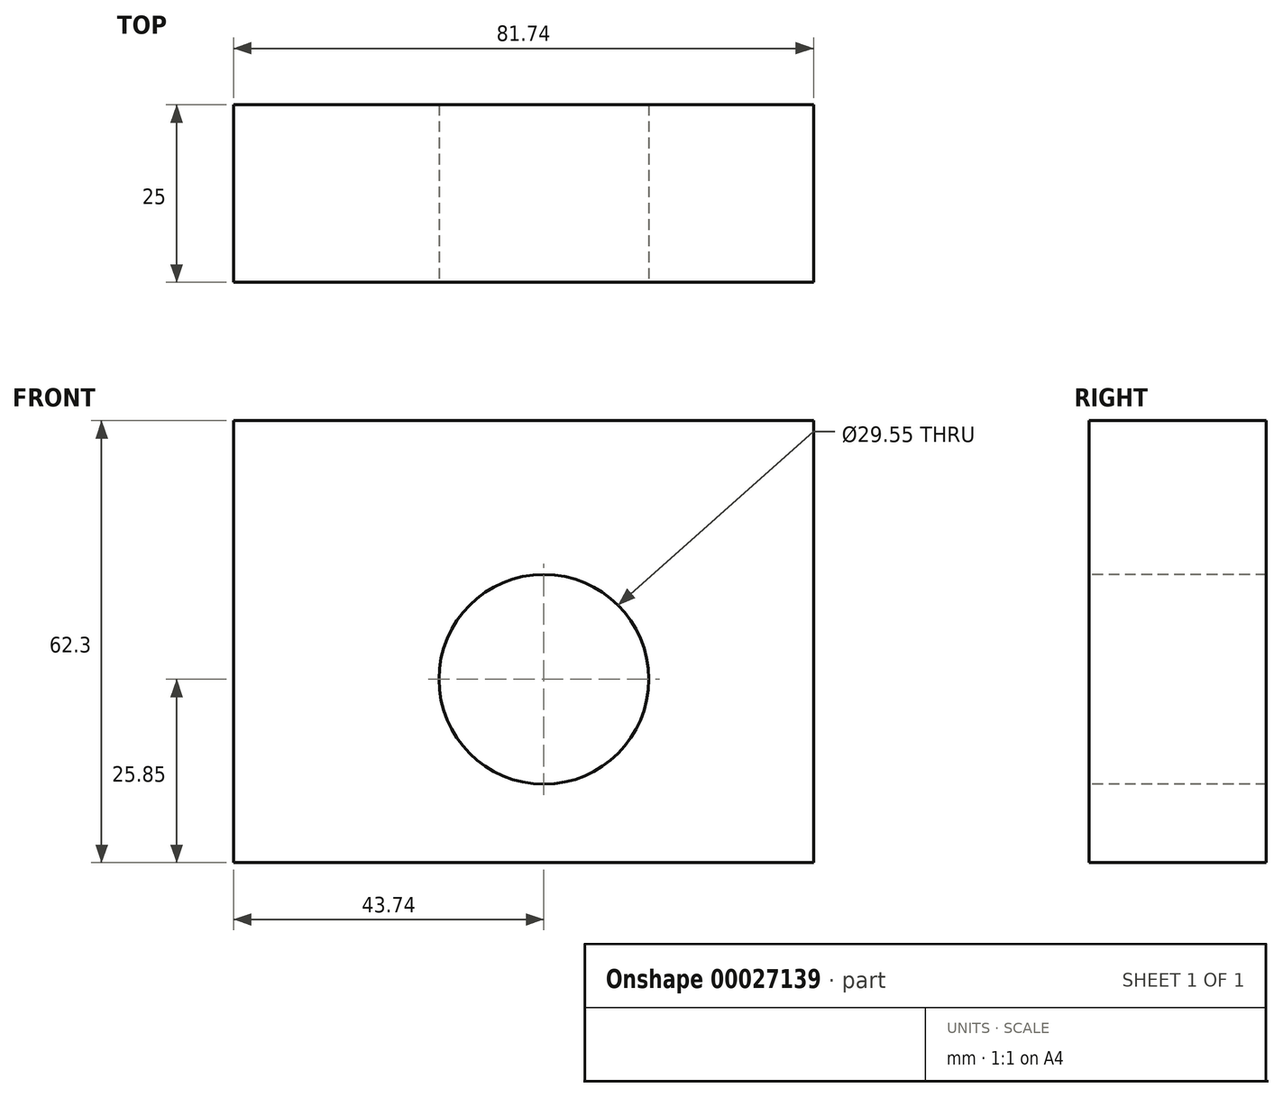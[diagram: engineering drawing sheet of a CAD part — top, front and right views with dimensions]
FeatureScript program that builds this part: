
annotation { "Feature Type Name" : "Feature", "Feature Type Description" : "" }
export const myFeature = defineFeature(function(context is Context, id is Id, definition is map)
    precondition{}
    {
        {
            var Q0;
            Q0=qCreatedBy(makeId("Front.planeOp"),FACE);
            var sketch = newSketch(context, id + "F0", { "sketchPlane" : qUnion([Q0])});
            skLineSegment(sketch, "E0.bottom", {"start": v(-43.74, 36.45) * mm, "end": v(38, 36.45) * mm});
            skLineSegment(sketch, "E0.top", {"start": v(-43.74, -25.85) * mm, "end": v(38, -25.85) * mm});
            skLineSegment(sketch, "E0.left", {"start": v(-43.74, 36.45) * mm, "end": v(-43.74, -25.85) * mm});
            skLineSegment(sketch, "E0.right", {"start": v(38, 36.45) * mm, "end": v(38, -25.85) * mm});
            skSolve(sketch);
        }
        {
            var Q0;
            Q0=makeQuery(id+"F0.imprint","IMPRINT",FACE,{"disambiguationData":[TD([[makeQuery(id+"F0.imprint","IMPRINT",EDGE,{"derivedFrom":sQuery(id+"F0.wireOp",EDGE,"E0.bottom")}),-1.0]])]});
            extrude(context, id + "F1", {"entities" : qUnion([Q0]), "depth" : 25 * mm});
        }
        {
            var Q0;
            Q0=makeQuery(id+"F1.opExtrude","CAP_FACE",FACE,{"disambiguationData":[OSD([sQuery(id+"F0.wireOp",EDGE,"E0.bottom"),sQuery(id+"F0.wireOp",EDGE,"E0.top"),sQuery(id+"F0.wireOp",EDGE,"E0.left"),sQuery(id+"F0.wireOp",EDGE,"E0.right")])],"isStart":false});
            var sketch = newSketch(context, id + "F2", { "sketchPlane" : qUnion([Q0])});
            skCircle(sketch, "E1", {"center": v(0, 0) * mm, "radius": 14.78 * mm});
            skSolve(sketch);
        }
        {
            var Q0;
            Q0=makeQuery(id+"F2.imprint","IMPRINT",FACE,{"disambiguationData":[TD([[makeQuery(id+"F2.imprint","IMPRINT",EDGE,{"derivedFrom":sQuery(id+"F2.wireOp",EDGE,"E1")}),1.0]])]});
            extrude(context, id + "F3", {"entities" : qUnion([Q0]), "operationType" : NewBodyOperationType.REMOVE, "oppositeDirection" : true, "depth" : 25 * mm, "hasSecondDirection" : true, "secondDirectionOppositeDirection" : false, "secondDirectionDepth" : 25 * mm});
        }
    });
